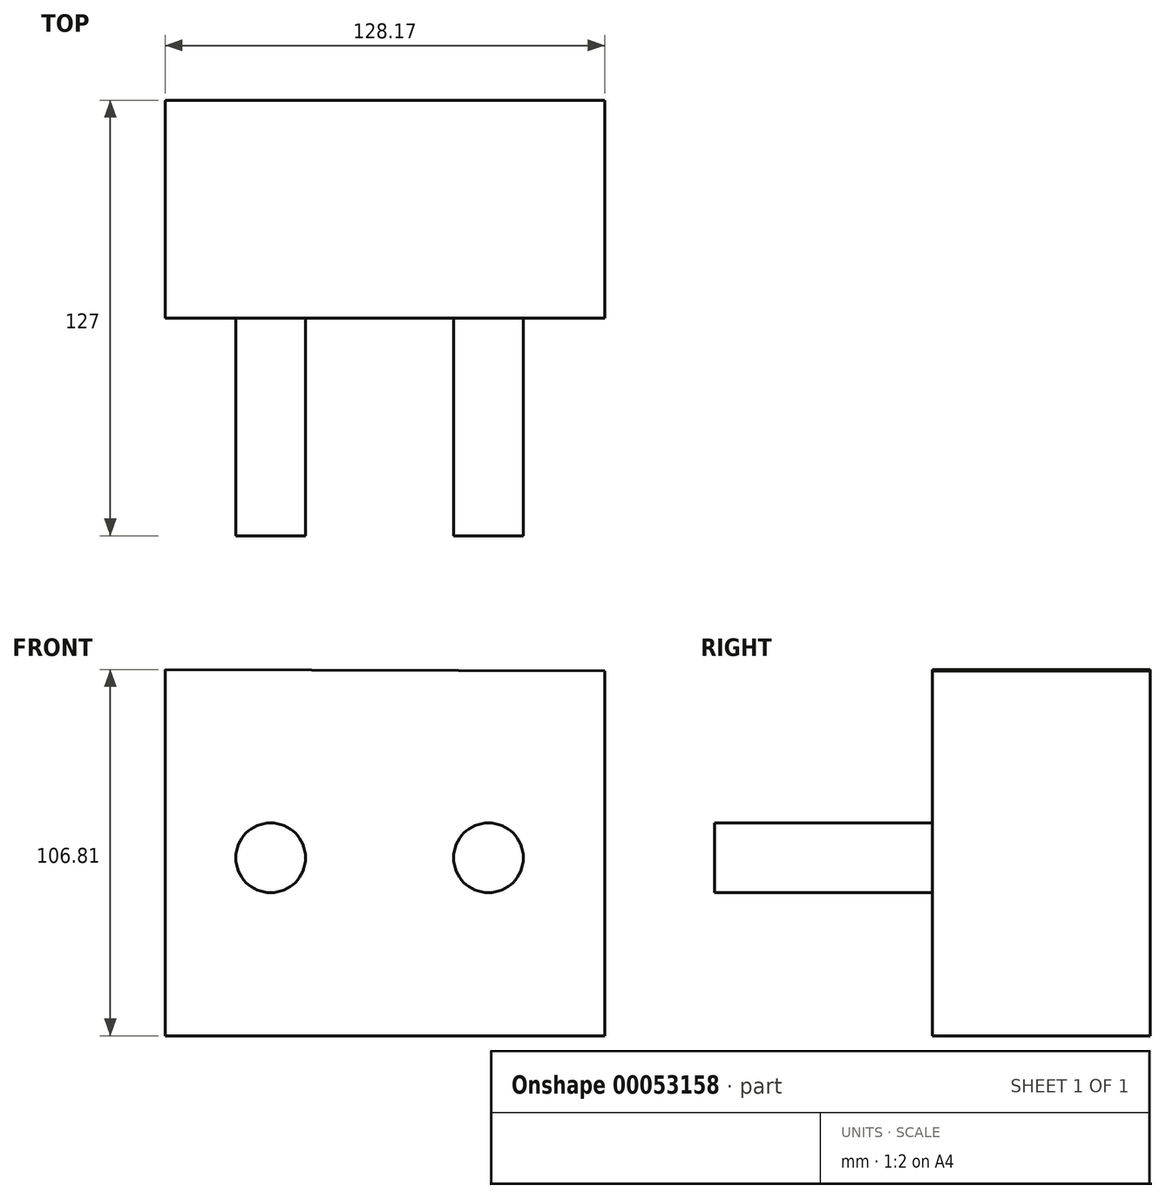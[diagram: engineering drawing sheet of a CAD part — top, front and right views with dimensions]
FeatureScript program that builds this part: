
annotation { "Feature Type Name" : "Feature", "Feature Type Description" : "" }
export const myFeature = defineFeature(function(context is Context, id is Id, definition is map)
    precondition{}
    {
        {
            var Q0;
            Q0=qCreatedBy(makeId("Front.planeOp"),FACE);
            var sketch = newSketch(context, id + "F0", { "sketchPlane" : qUnion([Q0])});
            skLineSegment(sketch, "E0", {"start": v(-62.51, 54.93) * mm, "end": v(-62.51, -51.88) * mm});
            skLineSegment(sketch, "E1", {"start": v(-62.51, -51.88) * mm, "end": v(65.66, -51.88) * mm});
            skLineSegment(sketch, "E2", {"start": v(65.66, -51.88) * mm, "end": v(65.66, 54.5) * mm});
            skLineSegment(sketch, "E3", {"start": v(65.66, 54.5) * mm, "end": v(-62.51, 54.93) * mm});
            skSolve(sketch);
        }
        {
            var Q0;
            Q0=makeQuery(id+"F0.imprint","IMPRINT",FACE,{"disambiguationData":[TD([[makeQuery(id+"F0.imprint","IMPRINT",EDGE,{"derivedFrom":sQuery(id+"F0.wireOp",EDGE,"E0")}),1.0]])]});
            extrude(context, id + "F1", {"entities" : qUnion([Q0]), "depth" : 63.5 * mm});
        }
        {
            var Q0;
            Q0=makeQuery(id+"F1.opExtrude","CAP_FACE",FACE,{"disambiguationData":[OSD([sQuery(id+"F0.wireOp",EDGE,"E0"),sQuery(id+"F0.wireOp",EDGE,"E1"),sQuery(id+"F0.wireOp",EDGE,"E2"),sQuery(id+"F0.wireOp",EDGE,"E3")])],"isStart":false});
            var sketch = newSketch(context, id + "F2", { "sketchPlane" : qUnion([Q0])});
            skLineSegment(sketch, "E4", {"start": v(0, 0) * mm, "end": v(-31.75, 0) * mm});
            skLineSegment(sketch, "E5", {"start": v(0, 0) * mm, "end": v(31.75, 0) * mm});
            skCircle(sketch, "E6", {"center": v(31.75, 0) * mm, "radius": 10.16 * mm});
            skCircle(sketch, "E7", {"center": v(-31.75, 0) * mm, "radius": 10.16 * mm});
            skSolve(sketch);
        }
        {
            var Q0;
            Q0=makeQuery(id+"F2.imprint","IMPRINT",FACE,{"disambiguationData":[TD([[makeQuery(id+"F2.imprint","IMPRINT",EDGE,{"derivedFrom":sQuery(id+"F2.wireOp",EDGE,"E7")}),1.0]])]});
            var Q1;
            Q1=makeQuery(id+"F2.imprint","IMPRINT",FACE,{"disambiguationData":[TD([[makeQuery(id+"F2.imprint","IMPRINT",EDGE,{"derivedFrom":sQuery(id+"F2.wireOp",EDGE,"E6")}),1.0]])]});
            extrude(context, id + "F3", {"entities" : qUnion([Q0, Q1]), "operationType" : NewBodyOperationType.ADD, "depth" : 63.5 * mm});
        }
    });
